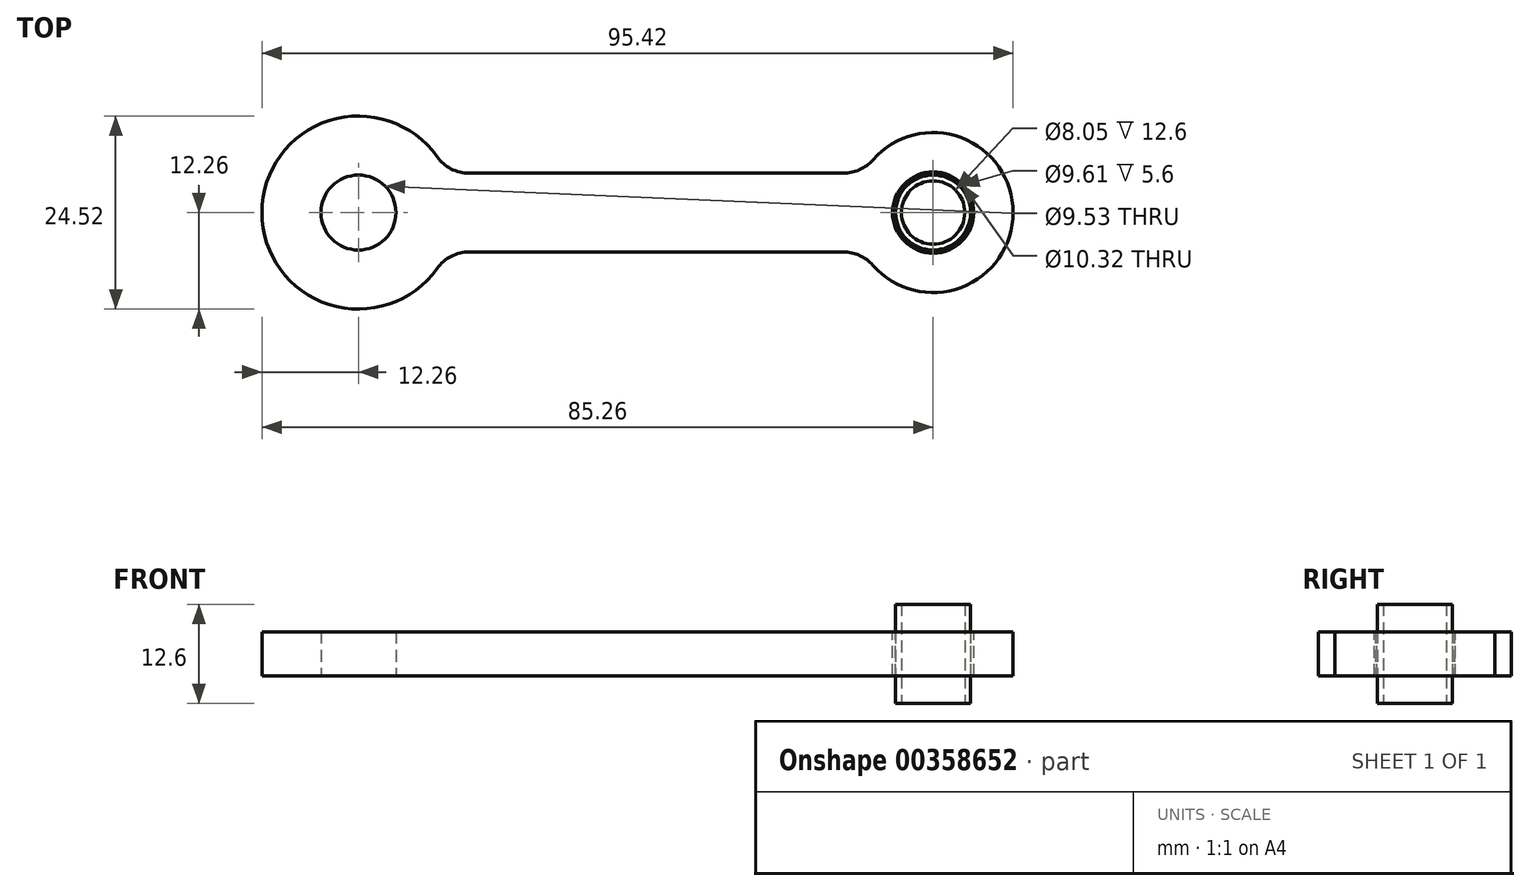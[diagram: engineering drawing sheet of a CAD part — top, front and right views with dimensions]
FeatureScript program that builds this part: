
annotation { "Feature Type Name" : "Feature", "Feature Type Description" : "" }
export const myFeature = defineFeature(function(context is Context, id is Id, definition is map)
    precondition{}
    {
        {
            var Q0;
            Q0=qCreatedBy(makeId("Top.planeOp"),FACE);
            var sketch = newSketch(context, id + "F0", { "sketchPlane" : qUnion([Q0])});
            skCircle(sketch, "E0", {"center": v(0, 0) * mm, "radius": 4.76 * mm});
            skArc(sketch, "E1", {"start": v(10, 7.1) * mm, "mid": v(-12.26, 0) * mm, "end": v(10, -7.1) * mm});
            skCircle(sketch, "E2", {"center": v(73, 0) * mm, "radius": 5.16 * mm});
            skLineSegment(sketch, "E3", {"start": v(0, 0) * mm, "end": v(73, 0) * mm, "construction": true});
            skLineSegment(sketch, "E4", {"start": v(14.07, -5) * mm, "end": v(61.6, -5) * mm});
            skArc(sketch, "E5", {"start": v(14.07, -5) * mm, "mid": v(11.78, -5.56) * mm, "end": v(10, -7.1) * mm});
            skLineSegment(sketch, "E6.trimOffspring", {"start": v(14.07, 5) * mm, "end": v(61.6, 5) * mm});
            skArc(sketch, "E7", {"start": v(10, 7.1) * mm, "mid": v(11.78, 5.56) * mm, "end": v(14.07, 5) * mm});
            skArc(sketch, "E8", {"start": v(65.36, -6.7) * mm, "mid": v(83.16, 0) * mm, "end": v(65.36, 6.7) * mm});
            skArc(sketch, "E9", {"start": v(61.6, 5) * mm, "mid": v(63.67, 5.45) * mm, "end": v(65.36, 6.7) * mm});
            skArc(sketch, "E10", {"start": v(65.36, -6.7) * mm, "mid": v(63.67, -5.45) * mm, "end": v(61.6, -5) * mm});
            skSolve(sketch);
        }
        {
            var Q0;
            Q0=makeQuery(id+"F0.imprint","IMPRINT",FACE,{"disambiguationData":[TD([[makeQuery(id+"F0.imprint","IMPRINT",EDGE,{"derivedFrom":sQuery(id+"F0.wireOp",EDGE,"E0")}),-1.0]])]});
            extrude(context, id + "F1", {"entities" : qUnion([Q0]), "depth" : 5.6 * mm, "offsetDistance" : 25 * mm});
        }
        {
            var Q0;
            Q0=makeQuery(id+"F1.opExtrude","CAP_FACE",FACE,{"disambiguationData":[OSD([sQuery(id+"F0.wireOp",EDGE,"E0"),sQuery(id+"F0.wireOp",EDGE,"E1"),sQuery(id+"F0.wireOp",EDGE,"E2"),sQuery(id+"F0.wireOp",EDGE,"E4"),sQuery(id+"F0.wireOp",EDGE,"E5"),sQuery(id+"F0.wireOp",EDGE,"E6.trimOffspring"),sQuery(id+"F0.wireOp",EDGE,"E7"),sQuery(id+"F0.wireOp",EDGE,"E8"),sQuery(id+"F0.wireOp",EDGE,"E9"),sQuery(id+"F0.wireOp",EDGE,"E10")])],"isStart":false});
            var sketch = newSketch(context, id + "F2", { "sketchPlane" : qUnion([Q0])});
            skCircle(sketch, "E11", {"center": v(73, 0) * mm, "radius": 5.16 * mm});
            skCircle(sketch, "E12", {"center": v(73, 0) * mm, "radius": 4.8 * mm});
            skSolve(sketch);
        }
        {
            var Q0;
            Q0=qSketchRegion(id+"F2",true);
            extrude(context, id + "F3", {"entities" : qUnion([Q0]), "depth" : 0 * mm, "offsetDistance" : 25 * mm, "hasSecondDirection" : true, "secondDirectionOppositeDirection" : true, "secondDirectionDepth" : 5.6 * mm});
        }
        {
            var Q0;
            Q0=makeQuery(id+"F1.opExtrude","CAP_FACE",FACE,{"disambiguationData":[OSD([sQuery(id+"F0.wireOp",EDGE,"E0"),sQuery(id+"F0.wireOp",EDGE,"E1"),sQuery(id+"F0.wireOp",EDGE,"E2"),sQuery(id+"F0.wireOp",EDGE,"E4"),sQuery(id+"F0.wireOp",EDGE,"E5"),sQuery(id+"F0.wireOp",EDGE,"E6.trimOffspring"),sQuery(id+"F0.wireOp",EDGE,"E7"),sQuery(id+"F0.wireOp",EDGE,"E8"),sQuery(id+"F0.wireOp",EDGE,"E9"),sQuery(id+"F0.wireOp",EDGE,"E10")])],"isStart":false});
            var sketch = newSketch(context, id + "F4", { "sketchPlane" : qUnion([Q0])});
            skCircle(sketch, "E13", {"center": v(73, 0) * mm, "radius": 4.76 * mm});
            skCircle(sketch, "E14", {"center": v(73, 0) * mm, "radius": 4.03 * mm});
            skSolve(sketch);
        }
        {
            var Q0;
            Q0=qSketchRegion(id+"F4",true);
            extrude(context, id + "F5", {"entities" : qUnion([Q0]), "depth" : 3.5 * mm, "offsetDistance" : 25 * mm, "hasSecondDirection" : true, "secondDirectionOppositeDirection" : true, "secondDirectionDepth" : (5.6 + 3.5) * mm});
        }
    });
